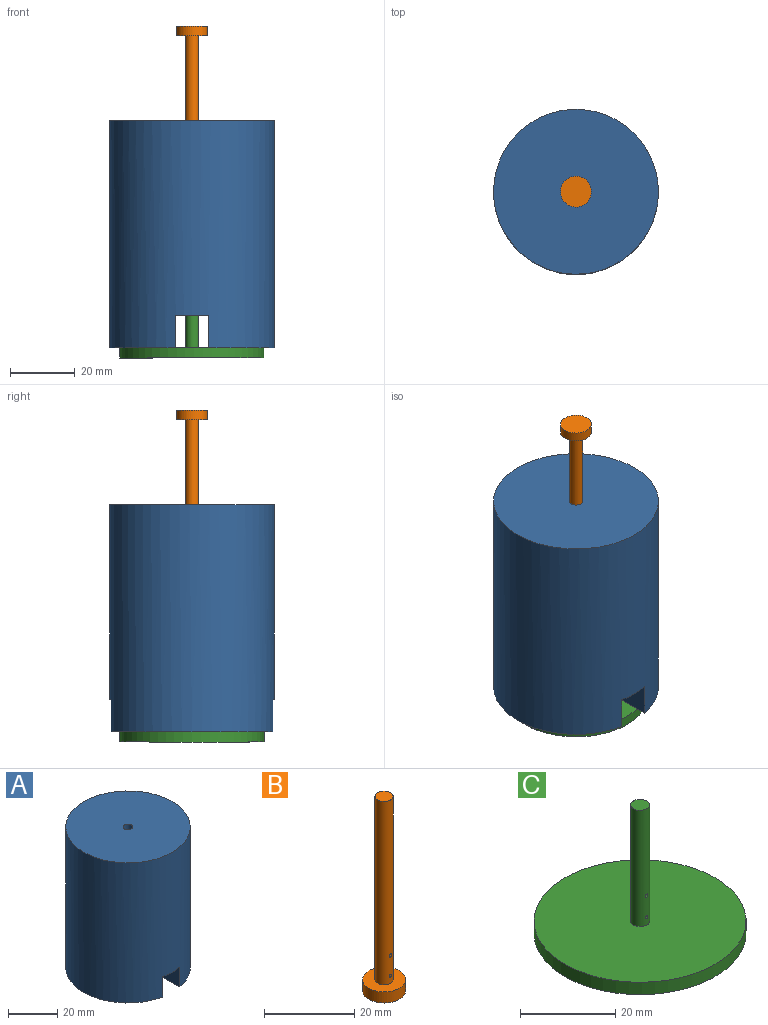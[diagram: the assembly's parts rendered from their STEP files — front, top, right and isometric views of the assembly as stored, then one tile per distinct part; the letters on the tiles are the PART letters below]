
ASSEMBLY  parts=3 mates=2
PART A: 8 faces, bbox 50.8x50.8x70 mm
  f0: plane 49.81x20.4mm, normal (0,0,-1), area 761.1mm2, adj f1,f5
  f1: cylinder r=25.4mm len=70mm, axis (0,0,-1), area 10970.2mm2, adj f0,f2,f3,f4,f5,f6
  f2: plane 50.8x50.8mm, normal (0,0,1), area 2014.3mm2, adj f1,f7
  f3: plane 49.81x20.4mm, normal (0,0,-1), area 761.1mm2, adj f1,f4
  f4: plane 49.81x10mm, normal (-1,0,0), area 498.1mm2, adj f1,f3,f6
  f5: plane 49.81x10mm, normal (1,0,0), area 498.1mm2, adj f0,f1,f6
  f6: plane 50.8x10mm, normal (0,0,-1), area 492.1mm2, adj f1,f4,f5,f7
  f7: cylinder r=2mm len=60mm, axis (0,0,1), area 754mm2, adj f2,f6
PART B: 9 faces, bbox 9.5x9.5x52.7 mm
  f0: cylinder r=2mm len=49.7mm, axis (0,0,-1), area 623.6mm2, adj f2,f4,f5,f7
  f1: cylinder r=4.76mm len=9.53mm, axis (0,0,-1), area 89.8mm2, adj f2,f3
  f2: plane 9.53x9.53mm, normal (0,0,1), area 58.7mm2, adj f0,f1
  f3: plane 9.53x9.53mm, normal (0,0,-1), area 71.3mm2, adj f1
  f4: plane 4x4mm, normal (0,0,1), area 12.6mm2, adj f0
  f5: cylinder r=0.4mm len=2mm, axis (0,-1,0), area 4.9mm2, adj f0,f6
  f6: cone r=0mm half-angle=59deg, axis (0,-1,0), area 0.6mm2, adj f5
  f7: cylinder r=0.4mm len=2mm, axis (0,-1,0), area 4.9mm2, adj f0,f8
  f8: cone r=0mm half-angle=59deg, axis (0,-1,0), area 0.6mm2, adj f7
PART C: 9 faces, bbox 44.5x44.5x33 mm
  f0: cylinder r=2mm len=29.83mm, axis (0,0,-1), area 373.8mm2, adj f2,f4,f5,f7
  f1: cylinder r=22.23mm len=44.45mm, axis (0,0,-1), area 443.4mm2, adj f2,f3
  f2: plane 44.45x44.45mm, normal (0,0,1), area 1539.2mm2, adj f0,f1
  f3: plane 44.45x44.45mm, normal (0,0,-1), area 1551.8mm2, adj f1
  f4: plane 4x4mm, normal (0,0,1), area 12.6mm2, adj f0
  f5: cylinder r=0.4mm len=2mm, axis (0,-1,0), area 4.9mm2, adj f0,f6
  f6: cone r=0mm half-angle=59deg, axis (0,-1,0), area 0.6mm2, adj f5
  f7: cylinder r=0.4mm len=2mm, axis (0,-1,0), area 4.9mm2, adj f0,f8
  f8: cone r=0mm half-angle=59deg, axis (0,-1,0), area 0.6mm2, adj f7
PLACE A rot(axis=(0.1,-0.99,-0.06),0deg) t=(0,0,0)mm fixed
PLACE B rot(axis=(-1,0,0),180deg) t=(0,0,99.13)mm
PLACE C rot(axis=(0,0,1),180deg) t=(0,0,-3.17)mm
MATE slider B.f0 <-> A.f1  axis (0,0,-1) through (0,0,46.43)mm
MATE fastened C.f1 <-> A.f1  axis (0,0,1) through (0,0,0)mm
